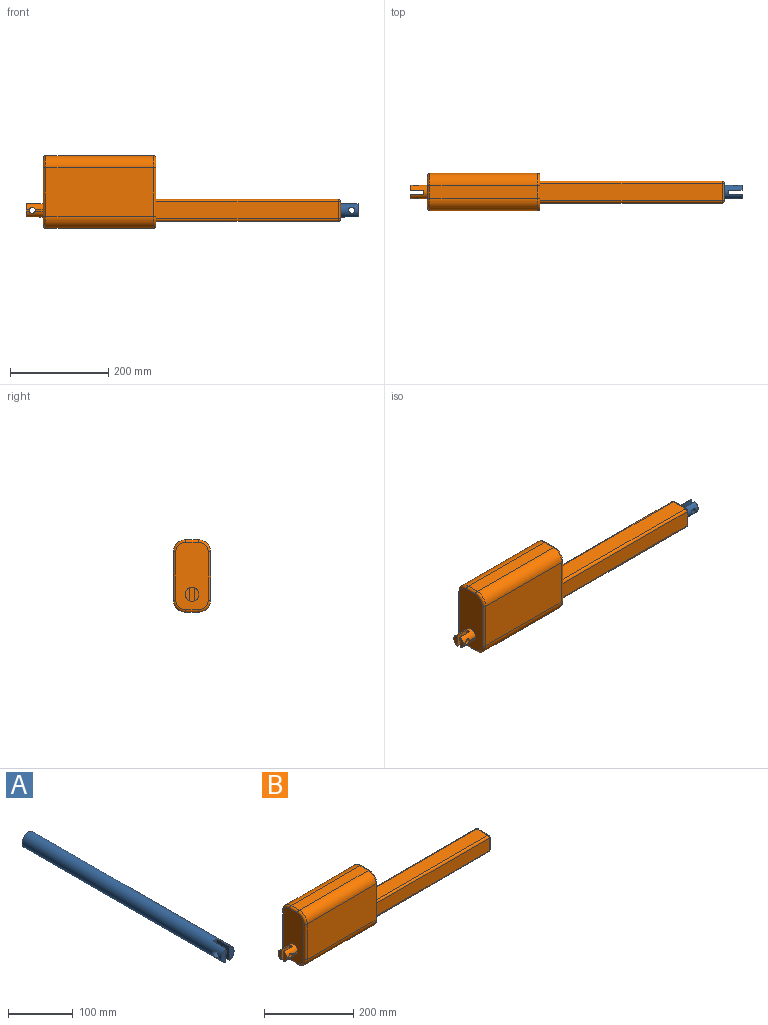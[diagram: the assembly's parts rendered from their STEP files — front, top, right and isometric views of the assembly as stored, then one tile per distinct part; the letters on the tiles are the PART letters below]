
ASSEMBLY  parts=2 mates=1
PART A: 12 faces, bbox 27.8x435.6x27.8 mm
  f0: plane 26.56x9.76mm, normal (0,-1,0), area 191.1mm2, adj f2,f6,f10
  f1: cylinder r=6.1mm len=12.2mm, axis (1,0,0), area 348.8mm2, adj f2,f3,f6,f10
  f2: cylinder r=13.9mm len=435.6mm, axis (0,1,0), area 37299.6mm2, adj f0,f1,f3,f4,f5,f6,f7,f8
  f3: plane 15.99x2.04mm, normal (1,0,0), area 32.5mm2, adj f1,f2,f7
  f4: plane 26.56x9.8mm, normal (0,-1,0), area 191.2mm2, adj f2,f9
  f5: plane 27.8x27.8mm, normal (0,1,0), area 607mm2, adj f2
  f6: plane 6.99x2.04mm, normal (1,0,0), area 14.1mm2, adj f0,f1,f2
  f7: plane 2.04x0.04mm, normal (0,-1,0), area 0.1mm2, adj f2,f3
  f8: cylinder r=6.1mm len=12.2mm, axis (1,0,0), area 349mm2, adj f2,f9
  f9: plane 27.5x26.56mm, normal (1,0,0), area 613.6mm2, adj f2,f4,f8,f11
  f10: plane 27.5x26.56mm, normal (-1,0,0), area 613.6mm2, adj f0,f1,f2,f11
  f11: plane 27.8x8.2mm, normal (0,-1,0), area 224.6mm2, adj f2,f9,f10
PART B: 56 faces, bbox 640.4x80.1x152.1 mm
  f0: plane 26.56x9.72mm, normal (-1,0,0), area 191mm2, adj f2,f11,f54
  f1: cylinder r=6.1mm len=12.2mm, axis (0,-1,0), area 348.6mm2, adj f2,f3,f11,f54
  f2: cylinder r=13.9mm len=35.6mm, axis (1,0,0), area 2342.7mm2, adj f0,f1,f3,f5,f10,f11,f12,f13
  f3: plane 16.09x3mm, normal (0,-1,0), area 47.9mm2, adj f1,f2,f12
  f4: plane 219x26mm, normal (0,0,1), area 5694mm2, adj f20,f22,f26,f34
  f5: plane 138x66mm, normal (-1,0,0), area 8157.6mm2, adj f2,f23,f24,f25,f26,f27,f28,f29
  f6: plane 219x26mm, normal (0,0,-1), area 5694mm2, adj f19,f21,f27,f35
  f7: plane 138x66mm, normal (1,0,0), area 6779.1mm2, adj f14,f15,f16,f17,f31,f32,f33,f34
  f8: plane 219x98mm, normal (0,-1,0), area 21462mm2, adj f21,f22,f30,f38
  f9: plane 219x98mm, normal (0,1,0), area 21462mm2, adj f19,f20,f23,f31
  f10: plane 26.56x9.8mm, normal (-1,0,0), area 191.2mm2, adj f2,f53
  f11: plane 7.09x3mm, normal (0,-1,0), area 20.9mm2, adj f0,f1,f2
  f12: plane 3x0.08mm, normal (-1,0,0), area 0.2mm2, adj f2,f3
  f13: cylinder r=6.1mm len=12.2mm, axis (0,-1,0), area 349mm2, adj f2,f53
  f14: plane 370.8x34.8mm, normal (0,-1,0), area 12903.8mm2, adj f7,f41,f47,f50
  f15: plane 370.8x34.8mm, normal (0,0,-1), area 12903.8mm2, adj f7,f44,f48,f50
  f16: plane 370.8x34.8mm, normal (0,1,0), area 12903.8mm2, adj f7,f39,f43,f44
  f17: plane 370.8x34.8mm, normal (0,0,1), area 12903.8mm2, adj f7,f39,f41,f42
  f18: plane 34.8x34.8mm, normal (1,0,0), area 604.1mm2, adj f42,f43,f47,f48,f51
  f19: cylinder r=25mm len=219mm, axis (1,0,0), area 8600.1mm2, adj f6,f9,f25,f33
  f20: cylinder r=25mm len=219mm, axis (-1,0,0), area 8600.1mm2, adj f4,f9,f24,f32
  f21: cylinder r=25mm len=219mm, axis (-1,0,0), area 8600.1mm2, adj f6,f8,f29,f37
  f22: cylinder r=25mm len=219mm, axis (1,0,0), area 8600.1mm2, adj f4,f8,f28,f36
  f23: cylinder r=5mm len=98mm, axis (0,0,-1), area 769.7mm2, adj f5,f9,f24,f25
  f24: torus R=20mm, axis (1,0,0), area 286mm2, adj f5,f20,f23,f26
  f25: torus R=20mm, axis (1,0,0), area 286mm2, adj f5,f19,f23,f27
  f26: cylinder r=5mm len=26mm, axis (0,-1,0), area 204.2mm2, adj f4,f5,f24,f28
  f27: cylinder r=5mm len=26mm, axis (0,1,0), area 204.2mm2, adj f5,f6,f25,f29
  f28: torus R=20mm, axis (1,0,0), area 286mm2, adj f5,f22,f26,f30
  f29: torus R=20mm, axis (1,0,0), area 286mm2, adj f5,f21,f27,f30
  f30: cylinder r=5mm len=98mm, axis (0,0,1), area 769.7mm2, adj f5,f8,f28,f29
  f31: cylinder r=5mm len=98mm, axis (0,0,1), area 769.7mm2, adj f7,f9,f32,f33
  f32: torus R=20mm, axis (1,0,0), area 286mm2, adj f7,f20,f31,f34
  f33: torus R=20mm, axis (1,0,0), area 286mm2, adj f7,f19,f31,f35
  f34: cylinder r=5mm len=26mm, axis (0,1,0), area 204.2mm2, adj f4,f7,f32,f36
  f35: cylinder r=5mm len=26mm, axis (0,-1,0), area 204.2mm2, adj f6,f7,f33,f37
  f36: torus R=20mm, axis (1,0,0), area 286mm2, adj f7,f22,f34,f38
  f37: torus R=20mm, axis (1,0,0), area 286mm2, adj f7,f21,f35,f38
  f38: cylinder r=5mm len=98mm, axis (0,0,-1), area 769.7mm2, adj f7,f8,f36,f37
  f39: cylinder r=5mm len=370.8mm, axis (-1,0,0), area 2912.3mm2, adj f7,f16,f17,f40
  f40: sphere r=5mm, area 39.3mm2, adj f39,f42,f43
  f41: cylinder r=5mm len=370.8mm, axis (1,0,0), area 2912.3mm2, adj f7,f14,f17,f45
  f42: cylinder r=5mm len=34.8mm, axis (0,1,0), area 273.3mm2, adj f17,f18,f40,f45
  f43: cylinder r=5mm len=34.8mm, axis (0,0,-1), area 273.3mm2, adj f16,f18,f40,f46
  f44: cylinder r=5mm len=370.8mm, axis (1,0,0), area 2912.3mm2, adj f7,f15,f16,f46
  f45: sphere r=5mm, area 39.3mm2, adj f41,f42,f47
  f46: sphere r=5mm, area 39.3mm2, adj f43,f44,f48
  f47: cylinder r=5mm len=34.8mm, axis (0,0,1), area 273.3mm2, adj f14,f18,f45,f49
  f48: cylinder r=5mm len=34.8mm, axis (0,-1,0), area 273.3mm2, adj f15,f18,f46,f49
  f49: sphere r=5mm, area 39.3mm2, adj f47,f48,f50
  f50: cylinder r=5mm len=370.8mm, axis (-1,0,0), area 2912.3mm2, adj f7,f14,f15,f49
  f51: cylinder r=13.9mm len=400mm, axis (1,0,0), area 34934.5mm2, adj f18,f52
  f52: plane 27.8x27.8mm, normal (1,0,0), area 607mm2, adj f51
  f53: plane 27.5x26.56mm, normal (0,-1,0), area 613.6mm2, adj f2,f10,f13,f55
  f54: plane 27.5x26.56mm, normal (0,1,0), area 613.6mm2, adj f0,f1,f2,f55
  f55: plane 27.8x8.2mm, normal (-1,0,0), area 224.6mm2, adj f2,f53,f54
PLACE A rot(axis=(0,0,1),90deg) t=(152.29,-104.52,13.89)mm fixed
PLACE B t=(-155.81,-104.52,51.29)mm
MATE slider B.f51 <-> A.f2  axis (-1,0,0) through (-65.51,-104.52,13.89)mm
